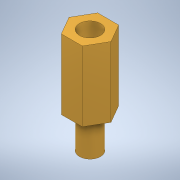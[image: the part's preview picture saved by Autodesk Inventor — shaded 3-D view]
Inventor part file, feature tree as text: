
AUTODESK INVENTOR PART (.ipt)
format: ipt  version: 2022 (Build 260153000, 153)  size: 112,128 bytes
history: native  units: mm
features: sketch x4, extrude x3
ambient origin geometry x8: Origin, YZ Plane, XZ Plane, XY Plane, X Axis, Y Axis, Z Axis, Center Point
bodies: Solid1 (feature_tree)
feature tree (7):
  sketch  "Sketch1"  dims[d0=6.0mm d1=10.0mm d2=0.0mm]
  sketch  "Sketch2"  dims[d3=3.0mm d4=3.0mm]
  extrude  "Extrusion1"  Depth=10.0mm TaperAngle=0.0deg
  sketch  "Sketch3"  dims[d5=5.0mm d6=0.0mm d7=10.0mm d8=0.0mm]
  sketch  "Sketch4"
  extrude  "Extrusion2"  Depth=3.0mm
  extrude  "Extrusion3"  Depth=10.0mm TaperAngle=0.0deg
